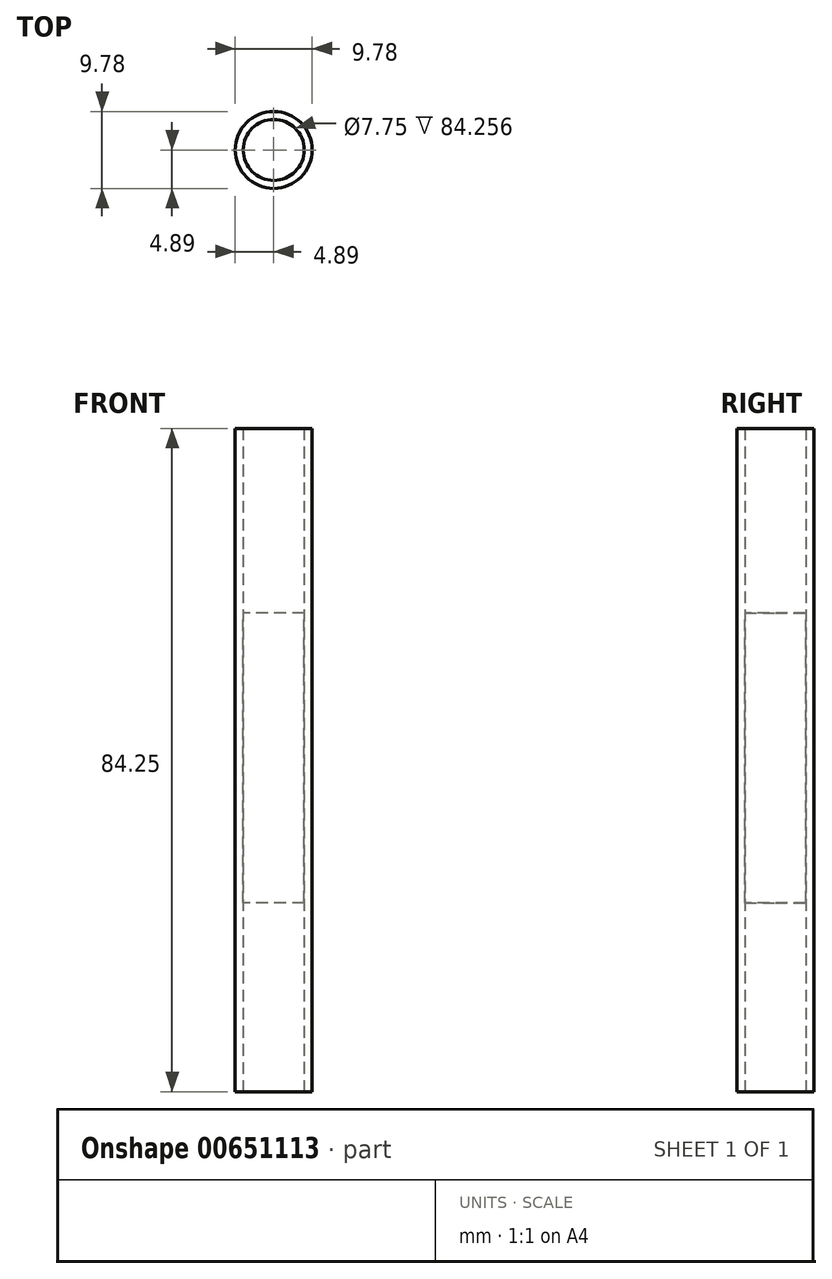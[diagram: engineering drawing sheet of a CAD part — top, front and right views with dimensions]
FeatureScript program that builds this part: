
annotation { "Feature Type Name" : "Feature", "Feature Type Description" : "" }
export const myFeature = defineFeature(function(context is Context, id is Id, definition is map)
    precondition{}
    {
        {
            var Q0;
            Q0=qCreatedBy(makeId("Right.planeOp"),FACE);
            var sketch = newSketch(context, id + "F0", { "sketchPlane" : qUnion([Q0])});
            skLineSegment(sketch, "E0", {"start": v(0, 23.44) * mm, "end": v(0, -60.81) * mm});
            skSolve(sketch);
        }
        {
            var Q0;
            Q0=sQuery(id+"F0.wireOp",EDGE,"E0");
            var Q1;
            Q1=sQuery(id+"F0.wireOp",VERTEX,"E0.start");
            cPlane(context, id + "F1", {"entities" : qUnion([Q0, Q1]), "cplaneType" : CPlaneType.LINE_POINT, "offset" : 25.4 * mm, "width" : 152.4 * mm, "height" : 152.4 * mm});
        }
        {
            var Q0;
            Q0=qCreatedBy(id+"F1.planeOp",FACE);
            var sketch = newSketch(context, id + "F2", { "sketchPlane" : qUnion([Q0])});
            skCircle(sketch, "E1", {"center": v(0, 0) * mm, "radius": 3.87 * mm});
            skCircle(sketch, "E2", {"center": v(0, 0) * mm, "radius": 4.89 * mm});
            skSolve(sketch);
        }
        {
            var Q0;
            Q0=makeQuery(id+"F2.imprint","IMPRINT",FACE,{"disambiguationData":[TD([[makeQuery(id+"F2.imprint","IMPRINT",EDGE,{"derivedFrom":sQuery(id+"F2.wireOp",EDGE,"E1")}),-1.0]])]});
            var Q1;
            Q1=sQuery(id+"F0.wireOp",EDGE,"E0");
            sweep(context, id + "F3", {"profiles" : qUnion([Q0]), "path" : qUnion([Q1])});
        }
        {
            var Q0;
            Q0=qCreatedBy(makeId("Top.planeOp"),FACE);
            var sketch = newSketch(context, id + "F4", { "sketchPlane" : qUnion([Q0])});
            skCircle(sketch, "E3", {"center": v(0, 0) * mm, "radius": 3.87 * mm});
            skSolve(sketch);
        }
        {
            var Q0;
            Q0=makeQuery(id+"F4.imprint","IMPRINT",FACE,{"disambiguationData":[TD([[makeQuery(id+"F4.imprint","IMPRINT",EDGE,{"derivedFrom":sQuery(id+"F4.wireOp",EDGE,"E3")}),1.0]])]});
            var Q1;
            Q1=makeQuery(id+"F3.opSweep","CAP_FACE",FACE,{"disambiguationData":[OSD([sQuery(id+"F0.wireOp",VERTEX,"E0.end"),sQuery(id+"F2.wireOp",EDGE,"E1"),sQuery(id+"F2.wireOp",EDGE,"E2")])],"isStart":false});
            extrude(context, id + "F5", {"entities" : qUnion([Q0]), "oppositeDirection" : true, "depth" : 36.8 * mm, "endBoundEntityFace" : qUnion([Q1]), "hasOffset" : true, "offsetDistance" : 23.44 * mm});
        }
    });
